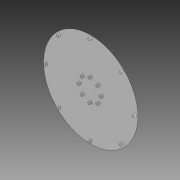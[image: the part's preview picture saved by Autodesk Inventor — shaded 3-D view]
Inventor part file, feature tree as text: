
AUTODESK INVENTOR PART (.ipt)
format: ipt  version: 2020 (Build 240168000, 168)  size: 120,832 bytes
history: native  units: mm
features: extrude x2, sketch x1, chamfer x1
ambient origin geometry x8: Origin, YZ Plane, XZ Plane, XY Plane, X Axis, Y Axis, Z Axis, Center Point
bodies: Solid1 (feature_tree)
feature tree (4):
  sketch  "Sketch1"  dims[d0=170.0mm d1=20.0mm d2=80.0mm d3=4.5mm d4=80.0mm d6=360.0deg d8=0.4mm d9=0.0mm d10=3.0mm d11=0.0mm d12=0.4mm d13=2.0mm d14=45.0deg]
  extrude  "Extrusion1"  Depth=20.0mm
  extrude  "Extrusion2"  Depth=80.0mm
  chamfer  "Chamfer1"  Distance=4.5mm
